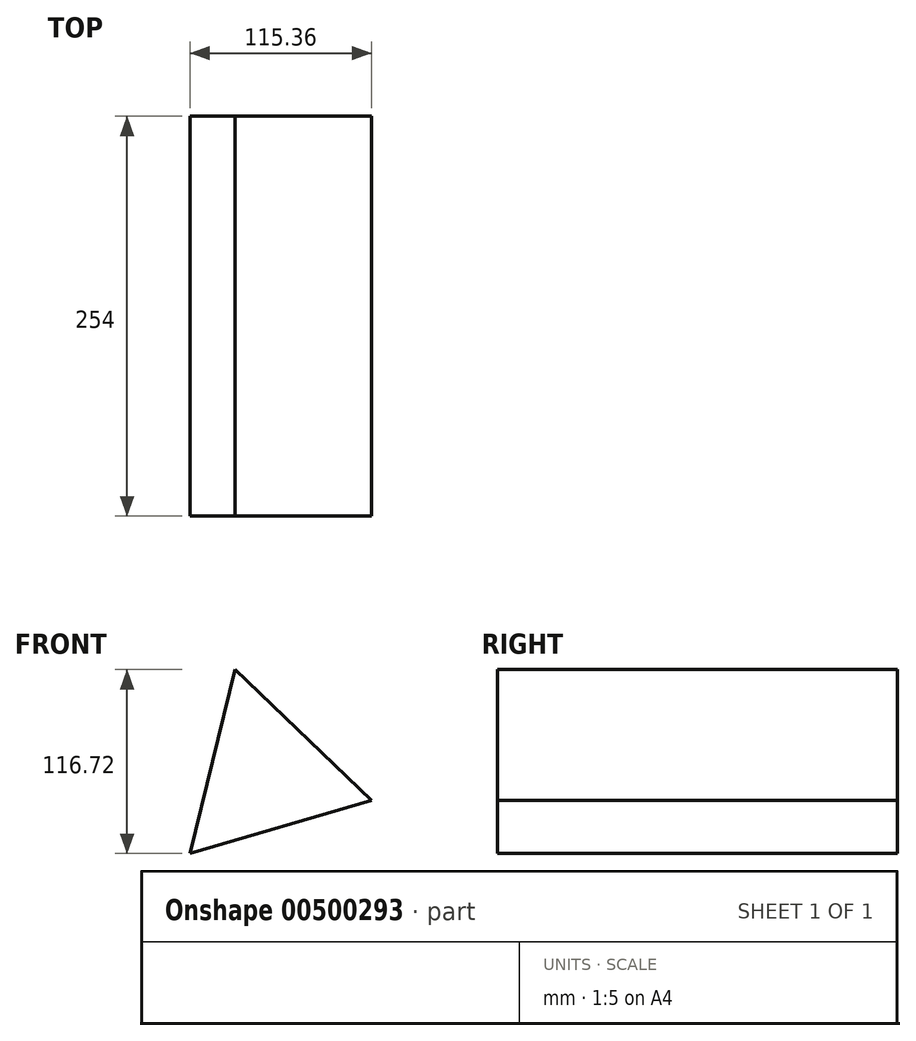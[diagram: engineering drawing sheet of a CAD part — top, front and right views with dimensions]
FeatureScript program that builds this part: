
annotation { "Feature Type Name" : "Feature", "Feature Type Description" : "" }
export const myFeature = defineFeature(function(context is Context, id is Id, definition is map)
    precondition{}
    {
        {
            var Q0;
            Q0=qCreatedBy(makeId("Front.planeOp"),FACE);
            var sketch = newSketch(context, id + "F0", { "sketchPlane" : qUnion([Q0])});
            skCircle(sketch, "E0.cCircle", {"center": v(0.77, 0) * mm, "radius": 69.38 * mm, "construction": true});
            skLineSegment(sketch, "E0.0", {"start": v(-18.65, 66.6) * mm, "end": v(68.16, -16.48) * mm});
            skLineSegment(sketch, "E0.1", {"start": v(68.16, -16.48) * mm, "end": v(-47.2, -50.12) * mm});
            skLineSegment(sketch, "E0.2", {"start": v(-47.2, -50.12) * mm, "end": v(-18.65, 66.6) * mm});
            skSolve(sketch);
        }
        {
            var Q0;
            Q0=makeQuery(id+"F0.imprint","IMPRINT",FACE,{"disambiguationData":[TD([[makeQuery(id+"F0.imprint","IMPRINT",EDGE,{"derivedFrom":sQuery(id+"F0.wireOp",EDGE,"E0.0")}),-1.0]])]});
            extrude(context, id + "F1", {"entities" : qUnion([Q0]), "endBound" : BoundingType.SYMMETRIC, "depth" : 254 * mm});
        }
    });
